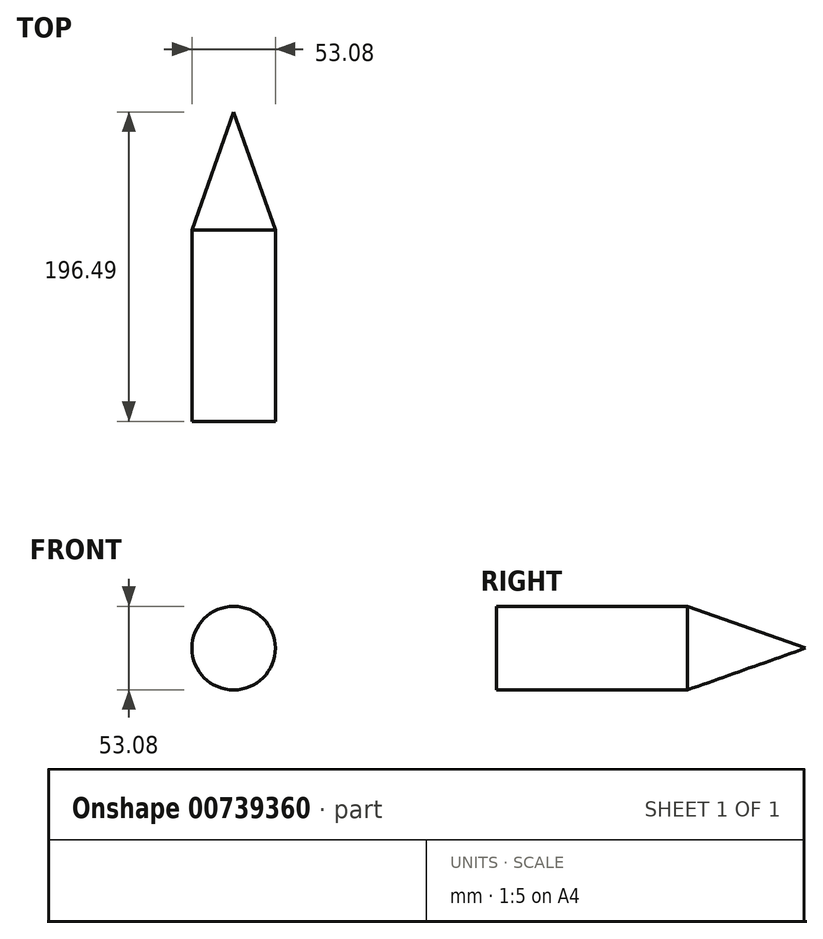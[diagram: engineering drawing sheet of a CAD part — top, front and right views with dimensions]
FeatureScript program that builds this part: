
annotation { "Feature Type Name" : "Feature", "Feature Type Description" : "" }
export const myFeature = defineFeature(function(context is Context, id is Id, definition is map)
    precondition{}
    {
        {
            var Q0;
            Q0=qCreatedBy(makeId("Front.planeOp"),FACE);
            var sketch = newSketch(context, id + "F0", { "sketchPlane" : qUnion([Q0])});
            skCircle(sketch, "E0", {"center": v(0, 0) * mm, "radius": 26.54 * mm});
            skSolve(sketch);
        }
        {
            var Q0;
            Q0=qCreatedBy(makeId("Top.planeOp"),FACE);
            var sketch = newSketch(context, id + "F1", { "sketchPlane" : qUnion([Q0])});
            skPoint(sketch, "E1", {"position": v(0, 75) * mm});
            skSolve(sketch);
        }
        {
            var Q0;
            Q0=makeQuery(id+"F0.imprint","IMPRINT",FACE,{"disambiguationData":[TD([[makeQuery(id+"F0.imprint","IMPRINT",EDGE,{"derivedFrom":sQuery(id+"F0.wireOp",EDGE,"E0")}),1.0]])]});
            var Q1;
            Q1=sQuery(id+"F1.wireOp",VERTEX,"E1");
            loft(context, id + "F2", {"sheetProfilesArray" : [{ "sheetProfileEntities" : qUnion([Q0]) }, { "sheetProfileEntities" : qUnion([Q1]) }]});
        }
        {
            var Q0;
            Q0=makeQuery(id+"F2.opLoft","CAP_FACE",FACE,{"disambiguationData":[OSD([makeQuery(id+"F0.imprint","IMPRINT",FACE,{"disambiguationData":[TD([[makeQuery(id+"F0.imprint","IMPRINT",EDGE,{"derivedFrom":sQuery(id+"F0.wireOp",EDGE,"E0")}),1.0]])]})])],"isStart":true});
            extrude(context, id + "F3", {"entities" : qUnion([Q0]), "operationType" : NewBodyOperationType.ADD, "depth" : 121.5 * mm, "offsetDistance" : 25 * mm});
        }
    });
